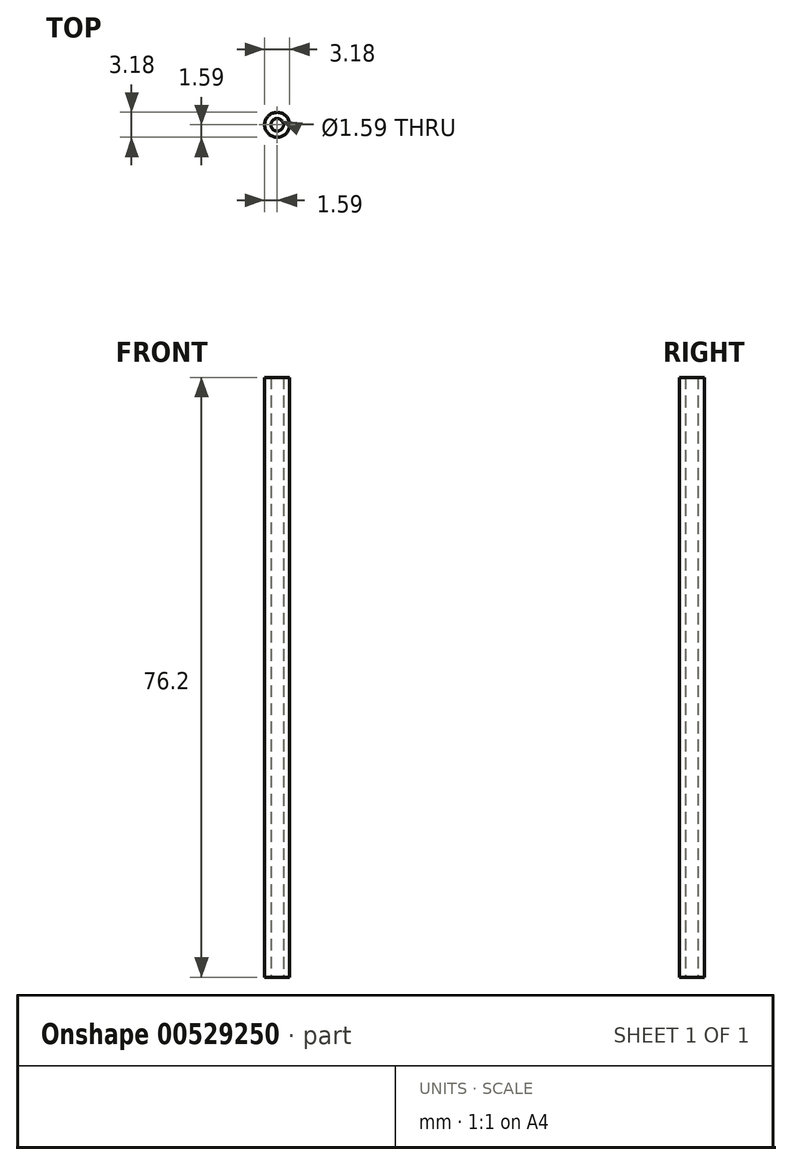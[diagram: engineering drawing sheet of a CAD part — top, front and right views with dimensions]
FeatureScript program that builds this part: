
annotation { "Feature Type Name" : "Feature", "Feature Type Description" : "" }
export const myFeature = defineFeature(function(context is Context, id is Id, definition is map)
    precondition{}
    {
        {
            var Q0;
            Q0=qCreatedBy(makeId("Top.planeOp"),FACE);
            var sketch = newSketch(context, id + "F0", { "sketchPlane" : qUnion([Q0])});
            skCircle(sketch, "E0", {"center": v(0, 0) * mm, "radius": 1.59 * mm});
            skCircle(sketch, "E1", {"center": v(0, 0) * mm, "radius": 0.8 * mm});
            skSolve(sketch);
        }
        {
            var Q0;
            Q0=qSketchRegion(id+"F0",true);
            extrude(context, id + "F1", {"entities" : qUnion([Q0]), "depth" : 76.2 * mm});
        }
    });
